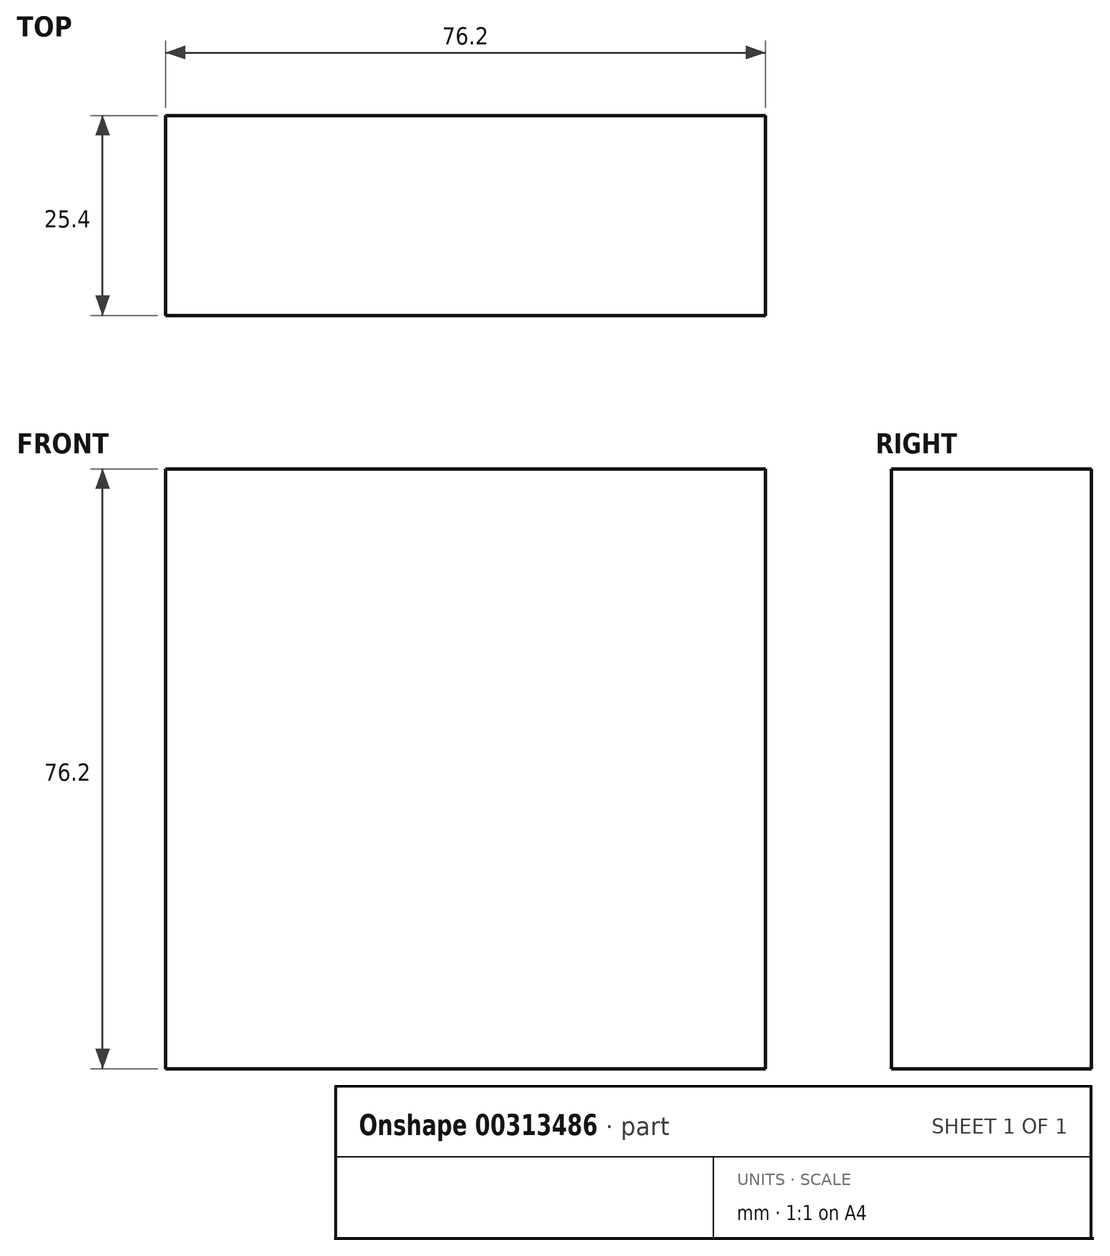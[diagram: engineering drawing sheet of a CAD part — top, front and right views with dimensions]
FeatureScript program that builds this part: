
annotation { "Feature Type Name" : "Feature", "Feature Type Description" : "" }
export const myFeature = defineFeature(function(context is Context, id is Id, definition is map)
    precondition{}
    {
        {
            var Q0;
            Q0=qCreatedBy(makeId("Front.planeOp"),FACE);
            var sketch = newSketch(context, id + "F0", { "sketchPlane" : qUnion([Q0])});
            skLineSegment(sketch, "E0", {"start": v(-49.73, -47.65) * mm, "end": v(26.47, -47.65) * mm});
            skLineSegment(sketch, "E1", {"start": v(26.47, -47.65) * mm, "end": v(26.47, 28.55) * mm});
            skLineSegment(sketch, "E2", {"start": v(26.47, 28.55) * mm, "end": v(-49.73, 28.55) * mm});
            skLineSegment(sketch, "E3", {"start": v(-49.73, 28.55) * mm, "end": v(-49.73, -47.65) * mm});
            skSolve(sketch);
        }
        {
            var Q0;
            Q0 = qSketchRegion(id + "F0", true);
            extrude(context, id + "F1", {"entities" : qUnion([Q0]), "depth" : 25.4 * mm});
        }
    });
